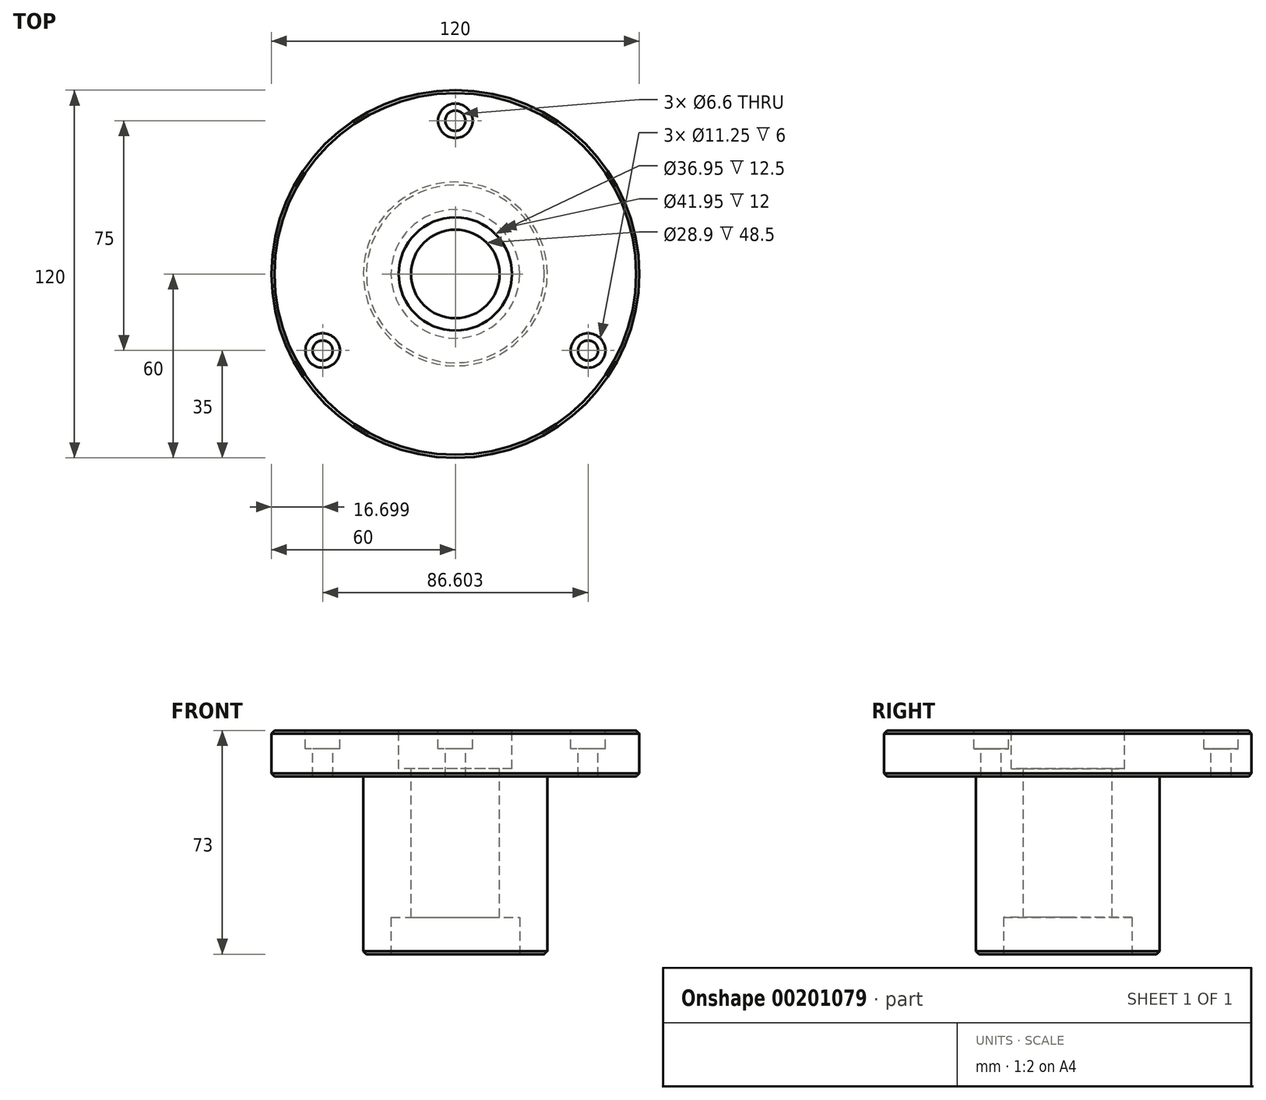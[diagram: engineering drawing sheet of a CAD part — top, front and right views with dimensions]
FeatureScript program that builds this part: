
annotation { "Feature Type Name" : "Feature", "Feature Type Description" : "" }
export const myFeature = defineFeature(function(context is Context, id is Id, definition is map)
    precondition{}
    {
        {
            var Q0;
            Q0=qCreatedBy(makeId("Top.planeOp"),FACE);
            var sketch = newSketch(context, id + "F0", { "sketchPlane" : qUnion([Q0])});
            skCircle(sketch, "E0", {"center": v(0, 0) * mm, "radius": 30 * mm});
            skSolve(sketch);
        }
        {
            var Q0;
            Q0=makeQuery(id+"F0.imprint","IMPRINT",FACE,{"disambiguationData":[TD([[makeQuery(id+"F0.imprint","IMPRINT",EDGE,{"derivedFrom":sQuery(id+"F0.wireOp",EDGE,"OFpQSDnw-eFdS-cNru-WySs-sgbIbi2b2W22")}),1.0]])]});
            var Q1;
            Q1=makeQuery(id+"F0.imprint","IMPRINT",FACE,{"disambiguationData":[TD([[makeQuery(id+"F0.imprint","IMPRINT",EDGE,{"derivedFrom":sQuery(id+"F0.wireOp",EDGE,"E0")}),1.0]])]});
            extrude(context, id + "F1", {"entities" : qUnion([Q0, Q1]), "depth" : 58 * mm});
        }
        {
            var Q0;
            Q0=makeQuery(id+"F1.opExtrude","CAP_FACE",FACE,{"disambiguationData":[OSD([sQuery(id+"F0.wireOp",EDGE,"E0")])],"isStart":false});
            var sketch = newSketch(context, id + "F2", { "sketchPlane" : qUnion([Q0])});
            skCircle(sketch, "E1", {"center": v(0, 0) * mm, "radius": 60 * mm});
            skSolve(sketch);
        }
        {
            var Q0;
            Q0=makeQuery(id+"F2.imprint","IMPRINT",FACE,{"disambiguationData":[TD([[makeQuery(id+"F2.imprint","IMPRINT",EDGE,{"derivedFrom":sQuery(id+"F2.wireOp",EDGE,"E1")}),1.0]])]});
            var Q1;
            Q1=makeQuery(id+"F2.imprint","IMPRINT",FACE,{"disambiguationData":[TD([[makeQuery(id+"F2.imprint","IMPRINT",EDGE,{"derivedFrom":makeQuery(id+"F1.opExtrude","CAP_EDGE",EDGE,{"disambiguationData":[OSD([sQuery(id+"F0.wireOp",EDGE,"E0")])],"isStart":false})}),1.0]])]});
            extrude(context, id + "F3", {"entities" : qUnion([Q0, Q1]), "operationType" : NewBodyOperationType.ADD, "depth" : 15 * mm});
        }
        {
            var Q0;
            Q0=makeQuery(id+"F3.opExtrude","CAP_FACE",FACE,{"disambiguationData":[OSD([sQuery(id+"F2.wireOp",EDGE,"E1")])],"isStart":false});
            var sketch = newSketch(context, id + "F4", { "sketchPlane" : qUnion([Q0])});
            skCircle(sketch, "E2", {"center": v(0, 0) * mm, "radius": 18.48 * mm});
            skPoint(sketch, "E3", {"position": v(0, 50) * mm});
            skPoint(sketch, "E4.1.0", {"position": v(-43.3, -25) * mm});
            skPoint(sketch, "E4.2.0", {"position": v(43.3, -25) * mm});
            skSolve(sketch);
        }
        {
            var Q0;
            Q0=makeQuery(id+"F4.imprint","IMPRINT",FACE,{"disambiguationData":[TD([[makeQuery(id+"F4.imprint","IMPRINT",EDGE,{"derivedFrom":sQuery(id+"F4.wireOp",EDGE,"E2")}),1.0]])]});
            extrude(context, id + "F5", {"entities" : qUnion([Q0]), "operationType" : NewBodyOperationType.REMOVE, "oppositeDirection" : true, "depth" : 12.5 * mm});
        }
        {
            var Q0;
            Q0=sQuery(id+"F4.wireOp",VERTEX,"E4.1.0");
            var Q1;
            Q1=sQuery(id+"F4.wireOp",VERTEX,"E3");
            var Q2;
            Q2=sQuery(id+"F4.wireOp",VERTEX,"E4.2.0");
            var Q3;
            Q3=makeQuery(id+"F1.opExtrude","SWEPT_BODY",BODY,{"disambiguationData":[OSD([sQuery(id+"F0.wireOp",EDGE,"E0")])]});
            hole(context, id + "F6", {"style" : HoleStyle.C_BORE, "endStyle" : HoleEndStyle.THROUGH, "standardTappedOrClearance" : lookupTablePath({ "standard" : "ISO", "fit" : "Normal", "size" : "M6", "type" : "Clearance" }), "standardBlindInLast" : lookupTablePath({ "standard" : "ISO", "fit" : "Standard", "size" : "M6", "type" : "Clearance" }), "holeDiameter" : 6.6 * mm, "cBoreDiameter" : 11.25 * mm, "cBoreDepth" : 6 * mm, "startFromSketch" : true, "locations" : qUnion([Q0, Q1, Q2]), "scope" : qUnion([Q3]), "isTappedThrough" : true});
        }
        {
            var Q0;
            Q0=makeQuery(id+"F1.opExtrude","CAP_FACE",FACE,{"disambiguationData":[OSD([sQuery(id+"F0.wireOp",EDGE,"E0")])],"isStart":true});
            var sketch = newSketch(context, id + "F7", { "sketchPlane" : qUnion([Q0])});
            skCircle(sketch, "E5", {"center": v(0, 0) * mm, "radius": 10 * mm, "construction": true});
            skCircle(sketch, "E6", {"center": v(0, 0) * mm, "radius": 20.98 * mm});
            skSolve(sketch);
        }
        {
            var Q0;
            Q0=makeQuery(id+"F7.imprint","IMPRINT",FACE,{"disambiguationData":[TD([[makeQuery(id+"F7.imprint","IMPRINT",EDGE,{"derivedFrom":sQuery(id+"F7.wireOp",EDGE,"E6")}),1.0]])]});
            var Q1;
            Q1=sQuery(id+"F7.wireOp",EDGE,"E6");
            extrude(context, id + "F8", {"entities" : qUnion([Q0]), "operationType" : NewBodyOperationType.REMOVE, "surfaceEntities" : qUnion([Q1]), "oppositeDirection" : true, "depth" : 12 * mm});
        }
        {
            var Q0;
            Q0=makeQuery(id+"F4.imprint","IMPRINT",FACE,{"disambiguationData":[TD([[makeQuery(id+"F4.imprint","IMPRINT",EDGE,{"derivedFrom":sQuery(id+"F4.wireOp",EDGE,"E2")}),-1.0]])]});
            var sketch = newSketch(context, id + "F9", { "sketchPlane" : qUnion([Q0])});
            skPoint(sketch, "E7", {"position": v(0, 0) * mm});
            skSolve(sketch);
        }
        {
            var Q0;
            Q0=sQuery(id+"F9.wireOp",VERTEX,"E7");
            var Q1;
            Q1=makeQuery(id+"F1.opExtrude","SWEPT_BODY",BODY,{"disambiguationData":[OSD([sQuery(id+"F0.wireOp",EDGE,"E0")])]});
            hole(context, id + "F10", {"style" : HoleStyle.SIMPLE, "endStyle" : HoleEndStyle.THROUGH, "holeDiameter" : 28.9 * mm, "startFromSketch" : true, "locations" : qUnion([Q0]), "scope" : qUnion([Q1]), "isTappedThrough" : true});
        }
        {
            var Q0;
            Q0=makeQuery(id+"F3.opExtrude","CAP_EDGE",EDGE,{"disambiguationData":[OSD([sQuery(id+"F2.wireOp",EDGE,"E1")])],"isStart":false});
            var Q1;
            Q1=makeQuery(id+"F3.opExtrude","CAP_EDGE",EDGE,{"disambiguationData":[OSD([sQuery(id+"F2.wireOp",EDGE,"E1")])],"isStart":true});
            var Q2;
            Q2=makeQuery(id+"F5.opExtrude","CAP_EDGE",EDGE,{"disambiguationData":[OSD([sQuery(id+"F4.wireOp",EDGE,"E2")])],"isStart":false});
            var Q3;
            Q3=makeQuery(id+"F1.opExtrude","CAP_EDGE",EDGE,{"disambiguationData":[OSD([sQuery(id+"F0.wireOp",EDGE,"E0")])],"isStart":true});
            var Q4;
            Q4=makeQuery(id+"F8.boolean.opBoolean","COPY",EDGE,{"derivedFrom":makeQuery(id+"F8.opExtrude","CAP_EDGE",EDGE,{"disambiguationData":[OSD([sQuery(id+"F7.wireOp",EDGE,"E6")])],"isStart":true})});
            var Q5;
            Q5=makeQuery(id+"F5.boolean.opBoolean","COPY",EDGE,{"derivedFrom":makeQuery(id+"F5.opExtrude","CAP_EDGE",EDGE,{"disambiguationData":[OSD([sQuery(id+"F4.wireOp",EDGE,"E2")])],"isStart":true})});
            chamfer(context, id + "F11", {"entities" : qUnion([Q0, Q1, Q2, Q3, Q4, Q5]), "width" : 1 * mm, "tangentPropagation" : true});
        }
    });
